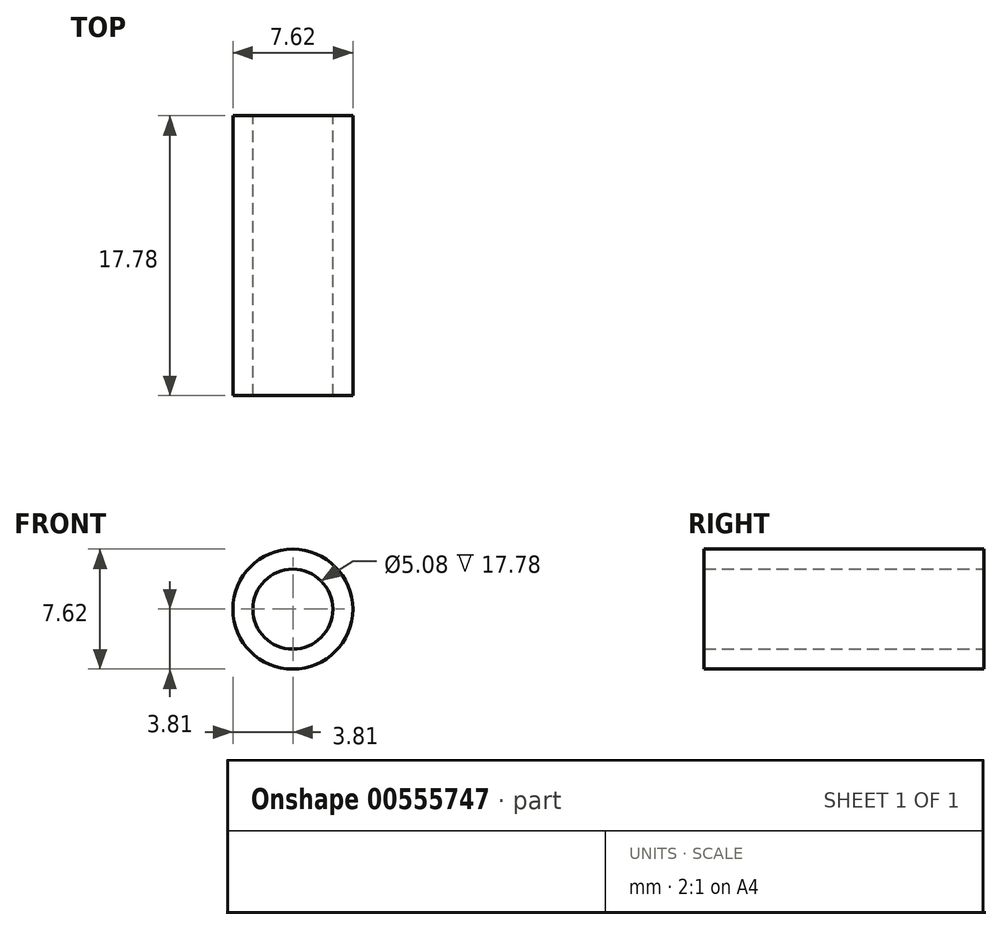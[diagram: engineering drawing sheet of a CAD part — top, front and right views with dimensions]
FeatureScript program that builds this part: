
annotation { "Feature Type Name" : "Feature", "Feature Type Description" : "" }
export const myFeature = defineFeature(function(context is Context, id is Id, definition is map)
    precondition{}
    {
        {
            var Q0;
            Q0=qCreatedBy(makeId("Front.planeOp"),FACE);
            var sketch = newSketch(context, id + "F0", { "sketchPlane" : qUnion([Q0])});
            skCircle(sketch, "E0", {"center": v(0, 0) * mm, "radius": 2.54 * mm});
            skCircle(sketch, "E1", {"center": v(0, 0) * mm, "radius": 3.81 * mm});
            skSolve(sketch);
        }
        {
            var Q0;
            Q0=makeQuery(id+"F0.imprint","IMPRINT",FACE,{"disambiguationData":[TD([[makeQuery(id+"F0.imprint","IMPRINT",EDGE,{"derivedFrom":sQuery(id+"F0.wireOp",EDGE,"E0")}),-1.0]])]});
            extrude(context, id + "F1", {"entities" : qUnion([Q0]), "depth" : 17.78 * mm, "offsetDistance" : 25.4 * mm});
        }
    });
